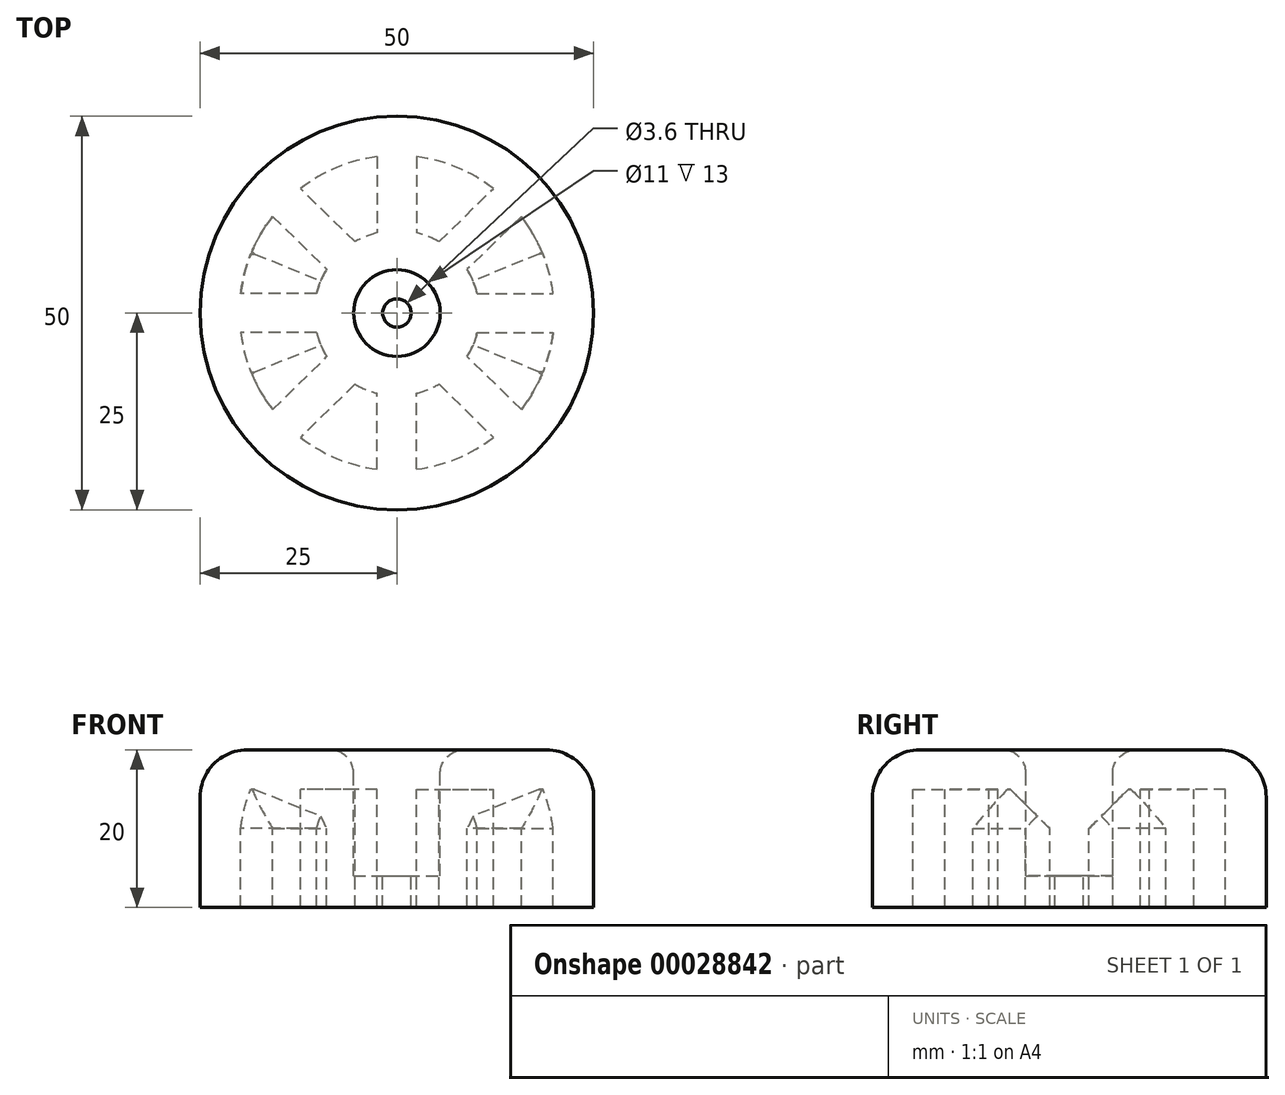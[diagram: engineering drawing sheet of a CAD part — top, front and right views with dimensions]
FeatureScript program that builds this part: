
annotation { "Feature Type Name" : "Feature", "Feature Type Description" : "" }
export const myFeature = defineFeature(function(context is Context, id is Id, definition is map)
    precondition{}
    {
        {
            var Q0;
            Q0=qCreatedBy(makeId("Top.planeOp"),FACE);
            var sketch = newSketch(context, id + "F0", { "sketchPlane" : qUnion([Q0])});
            skLineSegment(sketch, "E0", {"start": v(0, 0) * mm, "end": v(0, 20) * mm});
            skLineSegment(sketch, "E1", {"start": v(0, 0) * mm, "end": v(-20, 0) * mm});
            skLineSegment(sketch, "E2", {"start": v(-2.5, 19.84) * mm, "end": v(-2.5, 2.5) * mm});
            skLineSegment(sketch, "E3", {"start": v(-2.5, 2.5) * mm, "end": v(-19.84, 2.5) * mm});
            skArc(sketch, "E4", {"start": v(0, 25) * mm, "mid": v(-17.68, 17.68) * mm, "end": v(-25, 0) * mm});
            skArc(sketch, "E5", {"start": v(0, 20) * mm, "mid": v(-14.14, 14.14) * mm, "end": v(-20, 0) * mm});
            skLineSegment(sketch, "E6", {"start": v(0, 20) * mm, "end": v(0, 25) * mm});
            skLineSegment(sketch, "E7", {"start": v(-25, 0) * mm, "end": v(-20, 0) * mm});
            skArc(sketch, "E8", {"start": v(0, 5.5) * mm, "mid": v(-3.89, 3.89) * mm, "end": v(-5.5, 0) * mm});
            skArc(sketch, "E9", {"start": v(0, 1.8) * mm, "mid": v(-1.27, 1.27) * mm, "end": v(-1.8, 0) * mm});
            skArc(sketch, "E10", {"start": v(0, 10.5) * mm, "mid": v(-7.42, 7.42) * mm, "end": v(-10.5, 0) * mm});
            skLineSegment(sketch, "E11", {"start": v(-15.8, 12.26) * mm, "end": v(-8.91, 5.55) * mm});
            skLineSegment(sketch, "E12", {"start": v(-5.33, 9.04) * mm, "end": v(-12.26, 15.8) * mm});
            skLineSegment(sketch, "E13", {"start": v(-2.5, 10.2) * mm, "end": v(-5.33, 9.04) * mm, "construction": true});
            skLineSegment(sketch, "E14", {"start": v(-8.91, 5.55) * mm, "end": v(-10.2, 2.5) * mm, "construction": true});
            skLineSegment(sketch, "E15", {"start": v(-19.84, 2.5) * mm, "end": v(-15.8, 12.26) * mm, "construction": true});
            skLineSegment(sketch, "E16", {"start": v(-12.26, 15.8) * mm, "end": v(-2.5, 19.84) * mm, "construction": true});
            skSolve(sketch);
        }
        {
            var Q0;
            {var subQ1=sQuery(id+"F0.wireOp",EDGE,"E3");var subQ5=sQuery(id+"F0.wireOp",EDGE,"E5");var subQ6=makeQuery(id+"F0.imprint","INTERSECT",VERTEX,{"derivedFrom":[subQ1,subQ5]});Q0=makeQuery(id+"F0.imprint","IMPRINT",FACE,{"disambiguationData":[TD([[makeQuery(id+"F0.imprint","IMPRINT",EDGE,{"disambiguationData":[TD([[subQ6,1.0]])],"derivedFrom":subQ1}),1.0]])]});}
            var Q1;
            {var subQ0=sQuery(id+"F0.wireOp",EDGE,"E10");var subQ5=sQuery(id+"F0.wireOp",EDGE,"E2");var subQ6=makeQuery(id+"F0.imprint","INTERSECT",VERTEX,{"derivedFrom":[subQ5,subQ0]});Q1=makeQuery(id+"F0.imprint","IMPRINT",FACE,{"disambiguationData":[TD([[makeQuery(id+"F0.imprint","IMPRINT",EDGE,{"disambiguationData":[TD([[subQ6,-1.0]])],"derivedFrom":subQ5}),-1.0]])]});}
            var Q2;
            {var subQ3=sQuery(id+"F0.wireOp",EDGE,"E1");var subQ5=sQuery(id+"F0.wireOp",EDGE,"E8");var subQ7=makeQuery(id+"F0.imprint","INTERSECT",VERTEX,{"derivedFrom":[subQ3,subQ5]});Q2=makeQuery(id+"F0.imprint","IMPRINT",FACE,{"disambiguationData":[TD([[makeQuery(id+"F0.imprint","IMPRINT",EDGE,{"disambiguationData":[TD([[subQ7,-1.0]])],"derivedFrom":subQ3}),-1.0]])]});}
            var Q3;
            {var subQ0=sQuery(id+"F0.wireOp",EDGE,"E9");Q3=makeQuery(id+"F0.imprint","IMPRINT",FACE,{"disambiguationData":[TD([[makeQuery(id+"F0.imprint","IMPRINT",EDGE,{"derivedFrom":subQ0}),-1.0]])]});}
            var Q4;
            {var subQ1=sQuery(id+"F0.wireOp",EDGE,"E2");var subQ5=sQuery(id+"F0.wireOp",EDGE,"E5");var subQ6=makeQuery(id+"F0.imprint","INTERSECT",VERTEX,{"derivedFrom":[subQ1,subQ5]});Q4=makeQuery(id+"F0.imprint","IMPRINT",FACE,{"disambiguationData":[TD([[makeQuery(id+"F0.imprint","IMPRINT",EDGE,{"disambiguationData":[TD([[subQ6,-1.0]])],"derivedFrom":subQ1}),1.0]])]});}
            var Q5;
            {var subQ1=sQuery(id+"F0.wireOp",EDGE,"E11");Q5=makeQuery(id+"F0.imprint","IMPRINT",FACE,{"disambiguationData":[TD([[makeQuery(id+"F0.imprint","IMPRINT",EDGE,{"derivedFrom":subQ1}),1.0]])]});}
            var Q6;
            {var subQ3=sQuery(id+"F0.wireOp",EDGE,"E0");var subQ5=sQuery(id+"F0.wireOp",EDGE,"E8");var subQ7=makeQuery(id+"F0.imprint","INTERSECT",VERTEX,{"derivedFrom":[subQ3,subQ5]});Q6=makeQuery(id+"F0.imprint","IMPRINT",FACE,{"disambiguationData":[TD([[makeQuery(id+"F0.imprint","IMPRINT",EDGE,{"disambiguationData":[TD([[subQ7,-1.0]])],"derivedFrom":subQ3}),1.0]])]});}
            var Q7;
            Q7=makeQuery(id+"F0.imprint","IMPRINT",FACE,{"disambiguationData":[TD([[makeQuery(id+"F0.imprint","IMPRINT",EDGE,{"derivedFrom":sQuery(id+"F0.wireOp",EDGE,"E4")}),1.0]])]});
            var Q8;
            {var subQ1=sQuery(id+"F0.wireOp",EDGE,"E3");var subQ3=sQuery(id+"F0.wireOp",EDGE,"E2");var subQ5=makeQuery(id+"F0.imprint","INTERSECT",VERTEX,{"derivedFrom":[subQ3,subQ1]});Q8=makeQuery(id+"F0.imprint","IMPRINT",FACE,{"disambiguationData":[TD([[makeQuery(id+"F0.imprint","IMPRINT",EDGE,{"disambiguationData":[TD([[subQ5,1.0]])],"derivedFrom":subQ3}),-1.0]])]});}
            extrude(context, id + "F1", {"entities" : qUnion([Q0, Q1, Q2, Q3, Q4, Q5, Q6, Q7, Q8]), "depth" : 15 * mm});
        }
        {
            var Q0;
            {var subQ0=sQuery(id+"F0.wireOp",EDGE,"E9");Q0=makeQuery(id+"F0.imprint","IMPRINT",FACE,{"disambiguationData":[TD([[makeQuery(id+"F0.imprint","IMPRINT",EDGE,{"derivedFrom":subQ0}),-1.0]])]});}
            var Q1;
            {var subQ1=sQuery(id+"F0.wireOp",EDGE,"E3");var subQ3=sQuery(id+"F0.wireOp",EDGE,"E2");var subQ5=makeQuery(id+"F0.imprint","INTERSECT",VERTEX,{"derivedFrom":[subQ3,subQ1]});Q1=makeQuery(id+"F0.imprint","IMPRINT",FACE,{"disambiguationData":[TD([[makeQuery(id+"F0.imprint","IMPRINT",EDGE,{"disambiguationData":[TD([[subQ5,1.0]])],"derivedFrom":subQ3}),-1.0]])]});}
            extrude(context, id + "F2", {"entities" : qUnion([Q0, Q1]), "operationType" : NewBodyOperationType.REMOVE, "depth" : 11 * mm});
        }
        {
            var Q0;
            {var subQ1=sQuery(id+"F0.wireOp",EDGE,"E3");var subQ5=sQuery(id+"F0.wireOp",EDGE,"E5");var subQ6=makeQuery(id+"F0.imprint","INTERSECT",VERTEX,{"derivedFrom":[subQ1,subQ5]});Q0=makeQuery(id+"F0.imprint","IMPRINT",FACE,{"disambiguationData":[TD([[makeQuery(id+"F0.imprint","IMPRINT",EDGE,{"disambiguationData":[TD([[subQ6,1.0]])],"derivedFrom":subQ1}),1.0]])]});}
            var Q1;
            {var subQ0=sQuery(id+"F0.wireOp",EDGE,"E10");var subQ5=sQuery(id+"F0.wireOp",EDGE,"E2");var subQ6=makeQuery(id+"F0.imprint","INTERSECT",VERTEX,{"derivedFrom":[subQ5,subQ0]});Q1=makeQuery(id+"F0.imprint","IMPRINT",FACE,{"disambiguationData":[TD([[makeQuery(id+"F0.imprint","IMPRINT",EDGE,{"disambiguationData":[TD([[subQ6,-1.0]])],"derivedFrom":subQ5}),-1.0]])]});}
            var Q2;
            {var subQ3=sQuery(id+"F0.wireOp",EDGE,"E1");var subQ5=sQuery(id+"F0.wireOp",EDGE,"E8");var subQ7=makeQuery(id+"F0.imprint","INTERSECT",VERTEX,{"derivedFrom":[subQ3,subQ5]});Q2=makeQuery(id+"F0.imprint","IMPRINT",FACE,{"disambiguationData":[TD([[makeQuery(id+"F0.imprint","IMPRINT",EDGE,{"disambiguationData":[TD([[subQ7,-1.0]])],"derivedFrom":subQ3}),-1.0]])]});}
            var Q3;
            {var subQ0=sQuery(id+"F0.wireOp",EDGE,"E11");Q3=makeQuery(id+"F0.imprint","IMPRINT",FACE,{"disambiguationData":[TD([[makeQuery(id+"F0.imprint","IMPRINT",EDGE,{"derivedFrom":subQ0}),-1.0]])]});}
            var Q4;
            {var subQ1=sQuery(id+"F0.wireOp",EDGE,"E2");var subQ5=sQuery(id+"F0.wireOp",EDGE,"E5");var subQ6=makeQuery(id+"F0.imprint","INTERSECT",VERTEX,{"derivedFrom":[subQ1,subQ5]});Q4=makeQuery(id+"F0.imprint","IMPRINT",FACE,{"disambiguationData":[TD([[makeQuery(id+"F0.imprint","IMPRINT",EDGE,{"disambiguationData":[TD([[subQ6,-1.0]])],"derivedFrom":subQ1}),1.0]])]});}
            var Q5;
            {var subQ0=sQuery(id+"F0.wireOp",EDGE,"E12");Q5=makeQuery(id+"F0.imprint","IMPRINT",FACE,{"disambiguationData":[TD([[makeQuery(id+"F0.imprint","IMPRINT",EDGE,{"derivedFrom":subQ0}),-1.0]])]});}
            var Q6;
            {var subQ1=sQuery(id+"F0.wireOp",EDGE,"E11");Q6=makeQuery(id+"F0.imprint","IMPRINT",FACE,{"disambiguationData":[TD([[makeQuery(id+"F0.imprint","IMPRINT",EDGE,{"derivedFrom":subQ1}),1.0]])]});}
            var Q7;
            {var subQ3=sQuery(id+"F0.wireOp",EDGE,"E0");var subQ5=sQuery(id+"F0.wireOp",EDGE,"E8");var subQ7=makeQuery(id+"F0.imprint","INTERSECT",VERTEX,{"derivedFrom":[subQ3,subQ5]});Q7=makeQuery(id+"F0.imprint","IMPRINT",FACE,{"disambiguationData":[TD([[makeQuery(id+"F0.imprint","IMPRINT",EDGE,{"disambiguationData":[TD([[subQ7,-1.0]])],"derivedFrom":subQ3}),1.0]])]});}
            var Q8;
            Q8=makeQuery(id+"F0.imprint","IMPRINT",FACE,{"disambiguationData":[TD([[makeQuery(id+"F0.imprint","IMPRINT",EDGE,{"derivedFrom":sQuery(id+"F0.wireOp",EDGE,"E4")}),1.0]])]});
            extrude(context, id + "F3", {"entities" : qUnion([Q0, Q1, Q2, Q3, Q4, Q5, Q6, Q7, Q8]), "oppositeDirection" : true, "depth" : 5 * mm});
        }
        {
            var Q0;
            Q0=makeQuery(id+"F1.opExtrude","SWEPT_BODY",BODY,{"disambiguationData":[OSD([sQuery(id+"F0.wireOp",EDGE,"E0"),sQuery(id+"F0.wireOp",EDGE,"E1"),sQuery(id+"F0.wireOp",EDGE,"E2"),sQuery(id+"F0.wireOp",EDGE,"E3"),sQuery(id+"F0.wireOp",EDGE,"E4"),sQuery(id+"F0.wireOp",EDGE,"E5"),sQuery(id+"F0.wireOp",EDGE,"E6"),sQuery(id+"F0.wireOp",EDGE,"E7"),sQuery(id+"F0.wireOp",EDGE,"E9"),sQuery(id+"F0.wireOp",EDGE,"E10"),sQuery(id+"F0.wireOp",EDGE,"E11"),sQuery(id+"F0.wireOp",EDGE,"E12")])]});
            var Q1;
            Q1=makeQuery(id+"F3.opExtrude","SWEPT_BODY",BODY,{"disambiguationData":[OSD([sQuery(id+"F0.wireOp",EDGE,"E0"),sQuery(id+"F0.wireOp",EDGE,"E1"),sQuery(id+"F0.wireOp",EDGE,"E4"),sQuery(id+"F0.wireOp",EDGE,"E6"),sQuery(id+"F0.wireOp",EDGE,"E7"),sQuery(id+"F0.wireOp",EDGE,"E8")])]});
            booleanBodies(context, id + "F4", {"operationType" : BooleanOperationType.UNION, "tools" : qUnion([Q0, Q1])});
        }
        {
            var Q0;
            Q0=makeQuery(id+"F3.opExtrude","CAP_EDGE",EDGE,{"disambiguationData":[OSD([sQuery(id+"F0.wireOp",EDGE,"E4")])],"isStart":false});
            fillet(context, id + "F5", {"entities" : qUnion([Q0]), "radius" : 6 * mm, "tangentPropagation" : true, "allowEdgeOverflow" : false});
        }
        {
            var Q0;
            Q0=makeQuery(id+"F3.opExtrude","CAP_EDGE",EDGE,{"disambiguationData":[OSD([sQuery(id+"F0.wireOp",EDGE,"E8")])],"isStart":false});
            fillet(context, id + "F6", {"entities" : qUnion([Q0]), "radius" : 3 * mm, "tangentPropagation" : true, "allowEdgeOverflow" : false});
        }
        {
            var Q0;
            Q0=makeQuery(id+"F9.opPattern","COPY",EDGE,{"derivedFrom":makeQuery(id+"F1.opExtrude","CAP_EDGE",EDGE,{"disambiguationData":[OSD([sQuery(id+"F0.wireOp",EDGE,"E3")])],"isStart":true}),"instanceName":"1"});
            var Q1;
            Q1=makeQuery(id+"F1.opExtrude","CAP_EDGE",EDGE,{"disambiguationData":[OSD([sQuery(id+"F0.wireOp",EDGE,"E2")])],"isStart":true});
            var Q2;
            Q2=makeQuery(id+"F1.opExtrude","CAP_EDGE",EDGE,{"disambiguationData":[OSD([sQuery(id+"F0.wireOp",EDGE,"E12")])],"isStart":true});
            var Q3;
            Q3=makeQuery(id+"F1.opExtrude","CAP_EDGE",EDGE,{"disambiguationData":[OSD([sQuery(id+"F0.wireOp",EDGE,"E11")])],"isStart":true});
            var Q4;
            Q4=makeQuery(id+"F1.opExtrude","CAP_EDGE",EDGE,{"disambiguationData":[OSD([sQuery(id+"F0.wireOp",EDGE,"E3")])],"isStart":true});
            chamfer(context, id + "F7", {"entities" : qUnion([Q0, Q1, Q2, Q3, Q4]), "width" : 5 * mm, "tangentPropagation" : true});
        }
        {
            var Q0;
            Q0=makeQuery(id+"F1.opExtrude","SWEPT_BODY",BODY,{"disambiguationData":[OSD([sQuery(id+"F0.wireOp",EDGE,"E0"),sQuery(id+"F0.wireOp",EDGE,"E1"),sQuery(id+"F0.wireOp",EDGE,"E2"),sQuery(id+"F0.wireOp",EDGE,"E3"),sQuery(id+"F0.wireOp",EDGE,"E4"),sQuery(id+"F0.wireOp",EDGE,"E5"),sQuery(id+"F0.wireOp",EDGE,"E6"),sQuery(id+"F0.wireOp",EDGE,"E7"),sQuery(id+"F0.wireOp",EDGE,"E9"),sQuery(id+"F0.wireOp",EDGE,"E10"),sQuery(id+"F0.wireOp",EDGE,"E11"),sQuery(id+"F0.wireOp",EDGE,"E12")])]});
            var Q1;
            {var subQ0=sQuery(id+"F0.wireOp",EDGE,"E1");var subQ1=sQuery(id+"F0.wireOp",EDGE,"E7");Q1=makeQuery(id+"F4.opBoolean","MERGE",FACE,{"derivedFrom":[makeQuery(id+"F1.opExtrude","SWEPT_FACE",FACE,{"disambiguationData":[OSD([subQ0,subQ1])]}),makeQuery(id+"F3.opExtrude","SWEPT_FACE",FACE,{"disambiguationData":[OSD([subQ0,subQ1])]})]});}
            mirror(context, id + "F8", {"operationType" : NewBodyOperationType.ADD, "entities" : qUnion([Q0]), "mirrorPlane" : qUnion([Q1])});
        }
        {
            var Q0;
            Q0=makeQuery(id+"F1.opExtrude","SWEPT_BODY",BODY,{"disambiguationData":[OSD([sQuery(id+"F0.wireOp",EDGE,"E0"),sQuery(id+"F0.wireOp",EDGE,"E1"),sQuery(id+"F0.wireOp",EDGE,"E2"),sQuery(id+"F0.wireOp",EDGE,"E3"),sQuery(id+"F0.wireOp",EDGE,"E4"),sQuery(id+"F0.wireOp",EDGE,"E5"),sQuery(id+"F0.wireOp",EDGE,"E6"),sQuery(id+"F0.wireOp",EDGE,"E7"),sQuery(id+"F0.wireOp",EDGE,"E9"),sQuery(id+"F0.wireOp",EDGE,"E10"),sQuery(id+"F0.wireOp",EDGE,"E11"),sQuery(id+"F0.wireOp",EDGE,"E12")])]});
            var Q1;
            {var subQ0=sQuery(id+"F0.wireOp",EDGE,"E0");var subQ1=sQuery(id+"F0.wireOp",EDGE,"E6");Q1=makeQuery(id+"F8.opPattern","COPY",FACE,{"derivedFrom":makeQuery(id+"F4.opBoolean","MERGE",FACE,{"derivedFrom":[makeQuery(id+"F1.opExtrude","SWEPT_FACE",FACE,{"disambiguationData":[OSD([subQ0,subQ1])]}),makeQuery(id+"F3.opExtrude","SWEPT_FACE",FACE,{"disambiguationData":[OSD([subQ0,subQ1])]})]}),"instanceName":"1"});}
            mirror(context, id + "F9", {"operationType" : NewBodyOperationType.ADD, "entities" : qUnion([Q0]), "mirrorPlane" : qUnion([Q1])});
        }
        {
            var Q0;
            Q0=makeQuery(id+"F1.opExtrude","SWEPT_BODY",BODY,{"disambiguationData":[OSD([sQuery(id+"F0.wireOp",EDGE,"E0"),sQuery(id+"F0.wireOp",EDGE,"E1"),sQuery(id+"F0.wireOp",EDGE,"E2"),sQuery(id+"F0.wireOp",EDGE,"E3"),sQuery(id+"F0.wireOp",EDGE,"E4"),sQuery(id+"F0.wireOp",EDGE,"E5"),sQuery(id+"F0.wireOp",EDGE,"E6"),sQuery(id+"F0.wireOp",EDGE,"E7"),sQuery(id+"F0.wireOp",EDGE,"E9"),sQuery(id+"F0.wireOp",EDGE,"E10"),sQuery(id+"F0.wireOp",EDGE,"E11"),sQuery(id+"F0.wireOp",EDGE,"E12")])]});
            var Q1;
            Q1=sQuery(id+"F0.wireOp",EDGE,"E0");
            transform(context, id + "F10", {"entities" : qUnion([Q0]), "transformType" : TransformType.ROTATION, "transformAxis" : qUnion([Q1]), "angle" : 180 * degree, "makeCopy" : false});
        }
    });
